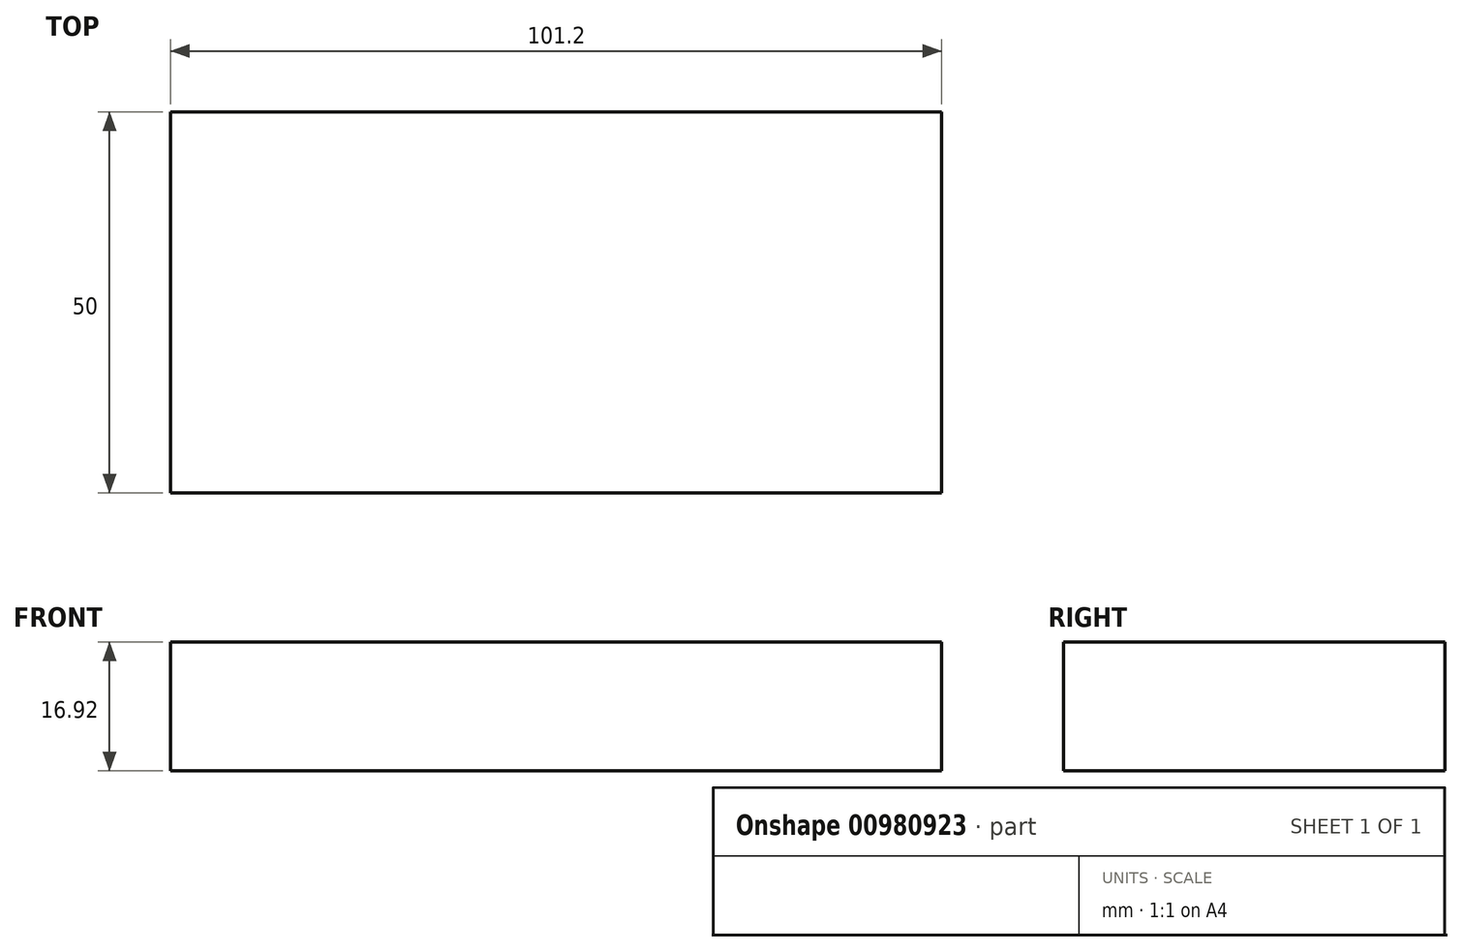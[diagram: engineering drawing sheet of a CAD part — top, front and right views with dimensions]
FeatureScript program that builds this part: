
annotation { "Feature Type Name" : "Feature", "Feature Type Description" : "" }
export const myFeature = defineFeature(function(context is Context, id is Id, definition is map)
    precondition{}
    {
        {
            var Q0;
            Q0=qCreatedBy(makeId("Front.planeOp"),FACE);
            var sketch = newSketch(context, id + "F0", { "sketchPlane" : qUnion([Q0])});
            skLineSegment(sketch, "E0.bottom", {"start": v(0, 0) * mm, "end": v(0, 0) * mm});
            skLineSegment(sketch, "E0.top", {"start": v(0, 0) * mm, "end": v(0, 0) * mm});
            skLineSegment(sketch, "E0.left", {"start": v(0, 0) * mm, "end": v(0, 0) * mm});
            skLineSegment(sketch, "E0.right", {"start": v(0, 0) * mm, "end": v(0, 0) * mm});
            skPoint(sketch, "E0.middle", {"position": v(0, 0) * mm});
            skLineSegment(sketch, "E1.bottom", {"start": v(50.6, 8.46) * mm, "end": v(-50.6, 8.46) * mm});
            skLineSegment(sketch, "E1.top", {"start": v(50.6, -8.46) * mm, "end": v(-50.6, -8.46) * mm});
            skLineSegment(sketch, "E1.left", {"start": v(50.6, 8.46) * mm, "end": v(50.6, -8.46) * mm});
            skLineSegment(sketch, "E1.right", {"start": v(-50.6, 8.46) * mm, "end": v(-50.6, -8.46) * mm});
            skSolve(sketch);
        }
        {
            var Q0;
            Q0 = qSketchRegion(id + "F0", true);
            extrude(context, id + "F1", {"entities" : qUnion([Q0]), "endBound" : BoundingType.SYMMETRIC, "depth" : 50 * mm, "offsetDistance" : 25.4 * mm});
        }
    });
